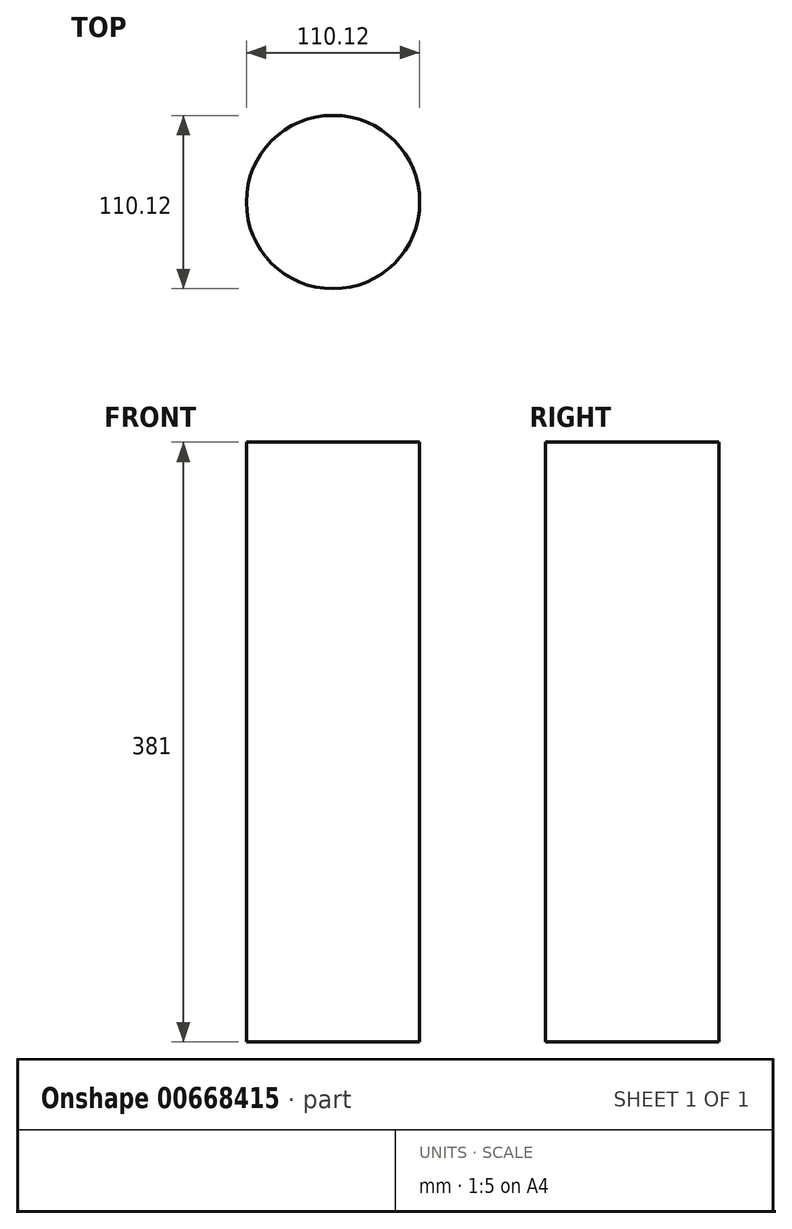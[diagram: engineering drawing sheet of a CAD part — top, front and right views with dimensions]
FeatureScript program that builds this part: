
annotation { "Feature Type Name" : "Feature", "Feature Type Description" : "" }
export const myFeature = defineFeature(function(context is Context, id is Id, definition is map)
    precondition{}
    {
        {
            var Q0;
            Q0=qCreatedBy(makeId("Top.planeOp"),FACE);
            var sketch = newSketch(context, id + "F0", { "sketchPlane" : qUnion([Q0])});
            skCircle(sketch, "E0", {"center": v(-5.6, 0) * mm, "radius": 55.06 * mm});
            skSolve(sketch);
        }
        {
            var Q0;
            Q0 = qSketchRegion(id + "F0", true);
            extrude(context, id + "F1", {"entities" : qUnion([Q0]), "depth" : 127 * mm, "offsetDistance" : 25.4 * mm});
        }
        {
            var Q0;
            Q0=makeQuery(id+"F1.opExtrude","CAP_FACE",FACE,{"disambiguationData":[OSD([sQuery(id+"F0.wireOp",EDGE,"E0")])],"isStart":false});
            extrude(context, id + "F2", {"entities" : qUnion([Q0]), "operationType" : NewBodyOperationType.ADD, "depth" : 254 * mm, "offsetDistance" : 25.4 * mm});
        }
    });
